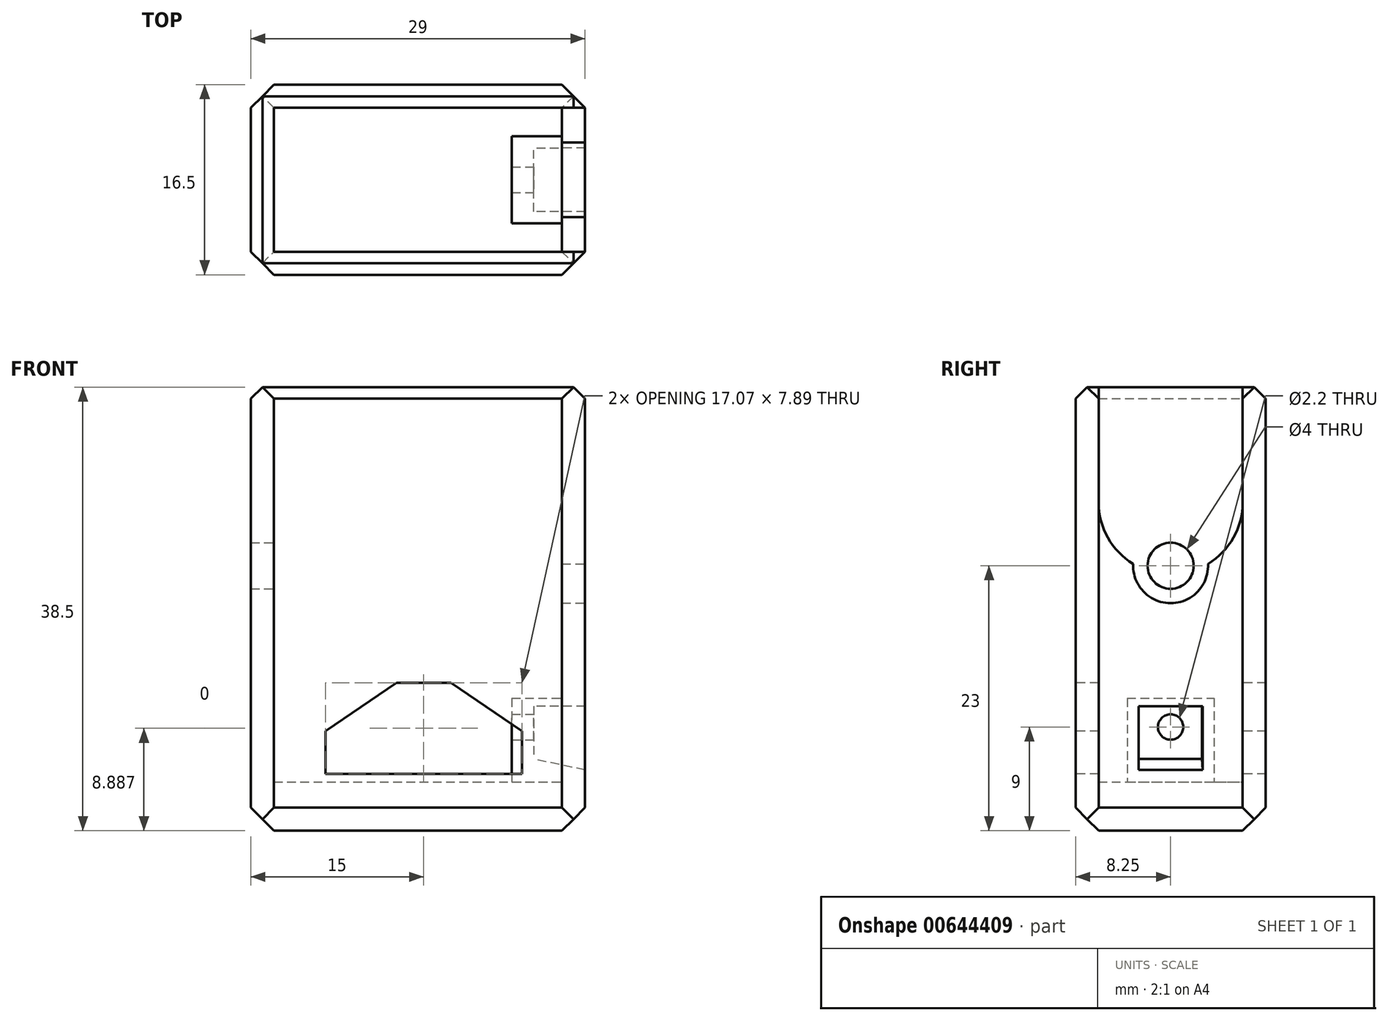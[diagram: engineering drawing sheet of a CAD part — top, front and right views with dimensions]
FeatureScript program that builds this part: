
annotation { "Feature Type Name" : "Feature", "Feature Type Description" : "" }
export const myFeature = defineFeature(function(context is Context, id is Id, definition is map)
    precondition{}
    {
        {
            var Q0;
            Q0=qCreatedBy(makeId("Top.planeOp"),FACE);
            var sketch = newSketch(context, id + "F0", { "sketchPlane" : qUnion([Q0])});
            skLineSegment(sketch, "E0.bottom", {"start": v(0, 0) * mm, "end": v(29, 0) * mm});
            skLineSegment(sketch, "E0.top", {"start": v(0, 16.5) * mm, "end": v(29, 16.5) * mm});
            skLineSegment(sketch, "E0.left", {"start": v(0, 0) * mm, "end": v(0, 16.5) * mm});
            skLineSegment(sketch, "E0.right", {"start": v(29, 0) * mm, "end": v(29, 16.5) * mm});
            skSolve(sketch);
        }
        {
            var Q0;
            Q0 = qSketchRegion(id + "F0", true);
            extrude(context, id + "F1", {"entities" : qUnion([Q0]), "depth" : 38.5 * mm, "offsetDistance" : 25 * mm});
        }
        {
            var Q0;
            Q0=makeQuery(id+"F1.opExtrude","CAP_FACE",FACE,{"disambiguationData":[OSD([sQuery(id+"F0.wireOp",EDGE,"E0.bottom"),sQuery(id+"F0.wireOp",EDGE,"E0.top"),sQuery(id+"F0.wireOp",EDGE,"E0.left"),sQuery(id+"F0.wireOp",EDGE,"E0.right")])],"isStart":false});
            shell(context, id + "F2", {"entities" : qUnion([Q0]), "thickness" : 2 * mm});
        }
        {
            var Q0;
            Q0=makeQuery(id+"F2.opShell","OFFSET_FACE",FACE,{"disambiguationData":[OSD([sQuery(id+"F0.wireOp",EDGE,"E0.bottom"),sQuery(id+"F0.wireOp",EDGE,"E0.top"),sQuery(id+"F0.wireOp",EDGE,"E0.left"),sQuery(id+"F0.wireOp",EDGE,"E0.right")])]});
            extrude(context, id + "F3", {"entities" : qUnion([Q0]), "operationType" : NewBodyOperationType.ADD, "depth" : 2.25 * mm, "offsetDistance" : 25 * mm});
        }
        {
            var Q0;
            Q0=makeQuery(id+"F1.opExtrude","SWEPT_EDGE",EDGE,{"disambiguationData":[OSD([sQuery(id+"F0.wireOp",EDGE,"E0.bottom"),sQuery(id+"F0.wireOp",EDGE,"E0.left")])]});
            var Q1;
            Q1=makeQuery(id+"F1.opExtrude","SWEPT_EDGE",EDGE,{"disambiguationData":[OSD([sQuery(id+"F0.wireOp",EDGE,"E0.bottom"),sQuery(id+"F0.wireOp",EDGE,"E0.right")])]});
            var Q2;
            Q2=makeQuery(id+"F1.opExtrude","SWEPT_EDGE",EDGE,{"disambiguationData":[OSD([sQuery(id+"F0.wireOp",EDGE,"E0.top"),sQuery(id+"F0.wireOp",EDGE,"E0.right")])]});
            var Q3;
            Q3=makeQuery(id+"F1.opExtrude","SWEPT_EDGE",EDGE,{"disambiguationData":[OSD([sQuery(id+"F0.wireOp",EDGE,"E0.top"),sQuery(id+"F0.wireOp",EDGE,"E0.left")])]});
            chamfer(context, id + "F4", {"entities" : qUnion([Q0, Q1, Q2, Q3]), "width" : 2 * mm, "tangentPropagation" : true});
        }
        {
            var Q0;
            Q0=makeQuery(id+"F1.opExtrude","CAP_EDGE",EDGE,{"disambiguationData":[OSD([sQuery(id+"F0.wireOp",EDGE,"E0.bottom")])],"isStart":true});
            var Q1;
            Q1=makeQuery(id+"F1.opExtrude","CAP_EDGE",EDGE,{"disambiguationData":[OSD([sQuery(id+"F0.wireOp",EDGE,"E0.left")])],"isStart":true});
            var Q2;
            Q2=makeQuery(id+"F1.opExtrude","CAP_EDGE",EDGE,{"disambiguationData":[OSD([sQuery(id+"F0.wireOp",EDGE,"E0.top")])],"isStart":true});
            var Q3;
            Q3=makeQuery(id+"F1.opExtrude","CAP_EDGE",EDGE,{"disambiguationData":[OSD([sQuery(id+"F0.wireOp",EDGE,"E0.right")])],"isStart":true});
            chamfer(context, id + "F5", {"entities" : qUnion([Q0, Q1, Q2, Q3]), "width" : 2 * mm, "tangentPropagation" : true});
        }
        {
            var Q0;
            Q0=makeQuery(id+"F1.opExtrude","CAP_EDGE",EDGE,{"disambiguationData":[OSD([sQuery(id+"F0.wireOp",EDGE,"E0.left")])],"isStart":false});
            var Q1;
            Q1=makeQuery(id+"F1.opExtrude","CAP_EDGE",EDGE,{"disambiguationData":[OSD([sQuery(id+"F0.wireOp",EDGE,"E0.top")])],"isStart":false});
            var Q2;
            Q2=makeQuery(id+"F1.opExtrude","CAP_EDGE",EDGE,{"disambiguationData":[OSD([sQuery(id+"F0.wireOp",EDGE,"E0.right")])],"isStart":false});
            var Q3;
            Q3=makeQuery(id+"F1.opExtrude","CAP_EDGE",EDGE,{"disambiguationData":[OSD([sQuery(id+"F0.wireOp",EDGE,"E0.bottom")])],"isStart":false});
            chamfer(context, id + "F6", {"entities" : qUnion([Q0, Q1, Q2, Q3]), "width" : 1 * mm, "tangentPropagation" : true});
        }
        {
            var Q0;
            Q0=makeQuery(id+"F1.opExtrude","SWEPT_FACE",FACE,{"disambiguationData":[OSD([sQuery(id+"F0.wireOp",EDGE,"E0.bottom")])]});
            var sketch = newSketch(context, id + "F7", { "sketchPlane" : qUnion([Q0])});
            skLineSegment(sketch, "E1", {"start": v(6.46, 4.94) * mm, "end": v(23.54, 4.94) * mm});
            skLineSegment(sketch, "E2", {"start": v(23.54, 4.94) * mm, "end": v(23.54, 8.66) * mm});
            skLineSegment(sketch, "E3", {"start": v(23.54, 8.66) * mm, "end": v(17.36, 12.83) * mm});
            skLineSegment(sketch, "E4", {"start": v(17.36, 12.83) * mm, "end": v(12.63, 12.83) * mm});
            skLineSegment(sketch, "E5", {"start": v(12.63, 12.83) * mm, "end": v(6.46, 8.66) * mm});
            skLineSegment(sketch, "E6", {"start": v(6.46, 8.66) * mm, "end": v(6.46, 4.94) * mm});
            skSolve(sketch);
        }
        {
            var Q0;
            Q0=makeQuery(id+"F7.imprint","IMPRINT",FACE,{"disambiguationData":[TD([[makeQuery(id+"F7.imprint","IMPRINT",EDGE,{"derivedFrom":sQuery(id+"F7.wireOp",EDGE,"E1")}),1.0]])]});
            extrude(context, id + "F8", {"entities" : qUnion([Q0]), "operationType" : NewBodyOperationType.REMOVE, "endBound" : BoundingType.THROUGH_ALL, "oppositeDirection" : true, "depth" : 25 * mm, "offsetDistance" : 25 * mm});
        }
        {
            var Q0;
            Q0=makeQuery(id+"F1.opExtrude","SWEPT_FACE",FACE,{"disambiguationData":[OSD([sQuery(id+"F0.wireOp",EDGE,"E0.right")])]});
            var sketch = newSketch(context, id + "F9", { "sketchPlane" : qUnion([Q0])});
            skCircle(sketch, "E7", {"center": v(8.25, 23) * mm, "radius": 3.25 * mm});
            skCircle(sketch, "E8", {"center": v(8.25, 28.5) * mm, "radius": 6.25 * mm});
            skLineSegment(sketch, "E9.bottom", {"start": v(2, 38.5) * mm, "end": v(14.5, 38.5) * mm});
            skLineSegment(sketch, "E9.top", {"start": v(2, 28.5) * mm, "end": v(14.5, 28.5) * mm});
            skLineSegment(sketch, "E9.left", {"start": v(2, 38.5) * mm, "end": v(2, 28.5) * mm});
            skLineSegment(sketch, "E9.right", {"start": v(14.5, 38.5) * mm, "end": v(14.5, 28.5) * mm});
            skSolve(sketch);
        }
        {
            var Q0;
            {var subQ0=sQuery(id+"F9.wireOp",EDGE,"E8");var subQ1=sQuery(id+"F9.wireOp",EDGE,"E7");var subQ2=makeQuery(id+"F9.imprint","INTERSECT",VERTEX,{"disambiguationData":[OD(0.0)],"derivedFrom":[subQ1,subQ0]});Q0=makeQuery(id+"F9.imprint","IMPRINT",FACE,{"disambiguationData":[TD([[makeQuery(id+"F9.imprint","IMPRINT",EDGE,{"disambiguationData":[TD([[subQ2,-1.0]])],"derivedFrom":subQ1}),1.0]])]});}
            var Q1;
            {var subQ0=sQuery(id+"F9.wireOp",EDGE,"E8");var subQ1=sQuery(id+"F9.wireOp",EDGE,"E7");var subQ2=makeQuery(id+"F9.imprint","INTERSECT",VERTEX,{"disambiguationData":[OD(0.0)],"derivedFrom":[subQ1,subQ0]});Q1=makeQuery(id+"F9.imprint","IMPRINT",FACE,{"disambiguationData":[TD([[makeQuery(id+"F9.imprint","IMPRINT",EDGE,{"disambiguationData":[TD([[subQ2,1.0]])],"derivedFrom":subQ1}),1.0]])]});}
            var Q2;
            {var subQ4=sQuery(id+"F9.wireOp",EDGE,"E9.top");Q2=makeQuery(id+"F9.imprint","IMPRINT",FACE,{"disambiguationData":[TD([[makeQuery(id+"F9.imprint","IMPRINT",EDGE,{"derivedFrom":subQ4}),-1.0]])]});}
            var Q3;
            {var subQ0=sQuery(id+"F9.wireOp",EDGE,"E9.top");Q3=makeQuery(id+"F9.imprint","IMPRINT",FACE,{"disambiguationData":[TD([[makeQuery(id+"F9.imprint","IMPRINT",EDGE,{"derivedFrom":subQ0}),1.0]])]});}
            var Q4;
            {var subQ3=sQuery(id+"F0.wireOp",EDGE,"E0.right");var subQ4=makeQuery(id+"F1.opExtrude","SWEPT_FACE",FACE,{"disambiguationData":[OSD([subQ3])]});var subQ8=makeQuery(id+"F6.opChamfer","BLEND_EDGE",EDGE,{"blendedFrom":[makeQuery(id+"F1.opExtrude","CAP_EDGE",EDGE,{"disambiguationData":[OSD([subQ3])],"isStart":false}),subQ4],"blendedInto":[subQ4]});Q4=makeQuery(id+"F9.imprint","IMPRINT",FACE,{"disambiguationData":[TD([[makeQuery(id+"F9.imprint","IMPRINT",EDGE,{"derivedFrom":subQ8}),1.0]])]});}
            var Q5;
            {var subQ0=sQuery(id+"F9.wireOp",EDGE,"E9.bottom");Q5=makeQuery(id+"F9.imprint","IMPRINT",FACE,{"disambiguationData":[TD([[makeQuery(id+"F9.imprint","IMPRINT",EDGE,{"derivedFrom":subQ0}),-1.0]])]});}
            extrude(context, id + "F10", {"entities" : qUnion([Q0, Q1, Q2, Q3, Q4, Q5]), "operationType" : NewBodyOperationType.REMOVE, "endBound" : BoundingType.UP_TO_NEXT, "oppositeDirection" : true, "depth" : 25 * mm, "offsetDistance" : 25 * mm});
        }
        {
            var Q0;
            Q0=makeQuery(id+"F2.opShell","OFFSET_FACE",FACE,{"disambiguationData":[OSD([sQuery(id+"F0.wireOp",EDGE,"E0.left")])]});
            var sketch = newSketch(context, id + "F11", { "sketchPlane" : qUnion([Q0])});
            skCircle(sketch, "E10", {"center": v(8.25, 23) * mm, "radius": 2 * mm});
            skSolve(sketch);
        }
        {
            var Q0;
            Q0=makeQuery(id+"F11.imprint","IMPRINT",FACE,{"disambiguationData":[TD([[makeQuery(id+"F11.imprint","IMPRINT",EDGE,{"derivedFrom":sQuery(id+"F11.wireOp",EDGE,"E10")}),1.0]])]});
            extrude(context, id + "F12", {"entities" : qUnion([Q0]), "operationType" : NewBodyOperationType.REMOVE, "endBound" : BoundingType.THROUGH_ALL, "oppositeDirection" : true, "depth" : 25 * mm, "offsetDistance" : 25 * mm});
        }
        {
            var Q0;
            Q0=makeQuery(id+"F2.opShell","OFFSET_FACE",FACE,{"disambiguationData":[OSD([sQuery(id+"F0.wireOp",EDGE,"E0.right")])]});
            var sketch = newSketch(context, id + "F13", { "sketchPlane" : qUnion([Q0])});
            skLineSegment(sketch, "E11.bottom", {"start": v(-4.48, 11.5) * mm, "end": v(-12.02, 11.5) * mm});
            skLineSegment(sketch, "E11.top", {"start": v(-4.48, 4.25) * mm, "end": v(-12.02, 4.25) * mm});
            skLineSegment(sketch, "E11.left", {"start": v(-4.48, 11.5) * mm, "end": v(-4.48, 4.25) * mm});
            skLineSegment(sketch, "E11.right", {"start": v(-12.02, 11.5) * mm, "end": v(-12.02, 4.25) * mm});
            skCircle(sketch, "E12", {"center": v(-8.25, 9) * mm, "radius": 1.1 * mm});
            skSolve(sketch);
        }
        {
            var Q0;
            Q0=makeQuery(id+"F13.imprint","IMPRINT",FACE,{"disambiguationData":[TD([[makeQuery(id+"F13.imprint","IMPRINT",EDGE,{"derivedFrom":sQuery(id+"F13.wireOp",EDGE,"E11.bottom")}),1.0]])]});
            extrude(context, id + "F14", {"entities" : qUnion([Q0]), "operationType" : NewBodyOperationType.ADD, "depth" : 4.35 * mm, "offsetDistance" : 25 * mm});
        }
        {
            var Q0;
            Q0=makeQuery(id+"F1.opExtrude","SWEPT_FACE",FACE,{"disambiguationData":[OSD([sQuery(id+"F0.wireOp",EDGE,"E0.right")])]});
            var sketch = newSketch(context, id + "F15", { "sketchPlane" : qUnion([Q0])});
            skLineSegment(sketch, "E13.bottom", {"start": v(5.48, 5.27) * mm, "end": v(11.02, 5.27) * mm});
            skLineSegment(sketch, "E13.top", {"start": v(5.48, 10.8) * mm, "end": v(11.02, 10.8) * mm});
            skLineSegment(sketch, "E13.left", {"start": v(5.48, 5.27) * mm, "end": v(5.48, 10.8) * mm});
            skLineSegment(sketch, "E13.right", {"start": v(11.02, 5.27) * mm, "end": v(11.02, 10.8) * mm});
            skSolve(sketch);
        }
        {
            var Q0;
            Q0=makeQuery(id+"F15.imprint","IMPRINT",FACE,{"disambiguationData":[TD([[makeQuery(id+"F15.imprint","IMPRINT",EDGE,{"derivedFrom":sQuery(id+"F15.wireOp",EDGE,"E13.bottom")}),-1.0]])]});
            cPlane(context, id + "F16", {"entities" : qUnion([Q0]), "cplaneType" : CPlaneType.OFFSET, "offset" : 4.45 * mm, "oppositeDirection" : true, "width" : 150 * mm, "height" : 150 * mm});
        }
        {
            var Q0;
            Q0=qCreatedBy(id+"F16.planeOp",FACE);
            var sketch = newSketch(context, id + "F17", { "sketchPlane" : qUnion([Q0])});
            skLineSegment(sketch, "E14.bottom", {"start": v(5.48, 10.8) * mm, "end": v(10.96, 10.8) * mm});
            skLineSegment(sketch, "E14.top", {"start": v(5.48, 6.22) * mm, "end": v(10.96, 6.22) * mm});
            skLineSegment(sketch, "E14.left", {"start": v(5.48, 10.8) * mm, "end": v(5.48, 6.22) * mm});
            skLineSegment(sketch, "E14.right", {"start": v(10.96, 10.8) * mm, "end": v(10.96, 6.22) * mm});
            skSolve(sketch);
        }
        {
            var Q1;
            Q1 = qSketchRegion(id + "F15", true);
            var Q2;
            Q2 = qSketchRegion(id + "F17", true);
            loft(context, id + "F18", {"operationType" : NewBodyOperationType.REMOVE, "sheetProfilesArray" : [{ "sheetProfileEntities" : qUnion([Q1]) }, { "sheetProfileEntities" : qUnion([Q2]) }]});
        }
    });
